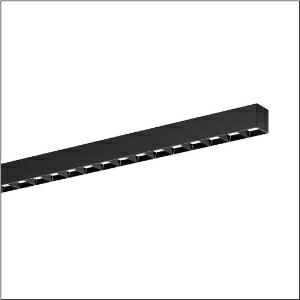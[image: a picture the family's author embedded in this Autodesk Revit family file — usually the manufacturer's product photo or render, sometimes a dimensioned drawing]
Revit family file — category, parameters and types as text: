
# Revit family: silica_r__21_51mx24dc3abb_157e
name_source: partatom
category: Lighting Fixtures
units: mm (PartAtom-declared; Revit-internal decimal feet)

## family parameters
Cut with Voids When Loaded = No
Host = Face
Light Source = No
Part Type = Normal
Room Calculation Point = No
Round Connector Dimension = Use Diameter
Shared = No

## types (1)
- --- (1 x LED, 10800 lm, 79 W, 3000K)
    Apparent Load = 79 VA
    CIE Flux Codes = 74 94 99 100 100
    Color Rendering = 80
    Color Temperature = 3000K
    Default Elevation = 1800 mm
    Description = Silica® 21, office luminaire, primary light control with darklight reflector, of PMMA, black, CAT 2 (L<= 3000cd/m²), light emission: direct distribution, primary light characteristic: asymmetric, installation type: surface-mounted, LED, rated luminous flux: 10.800lm, luminous efficacy: 137lm/W, light colour: 830, colour temperature: 3000K, with terminal, 3+2-pole, max. 2.5mm², mains connection: 220..240V, AC, 50/60Hz, rated input power: 79W, luminaire housing, of aluminium, jet black (RAL 9005), length: 3.004mm, width: 53mm, height: 53mm, protection rating (complete): IP20, insulation class (complete): insulation class I (protective earthing), certification: CE, permissible operating ambient temperature: 0..+35°C, standard: EN 50419, packaging unit: 1 piece
    Height = 0 mm  [stored 0 ft]
    Lamp = 1 x LED
    Lamp Light Flux = 10800 lm
    Lamp Power = 79 W
    Lamp count = 1
    Length = 3004 mm
    Luminous efficacy = 137 lm/W
    Manufacturer = Siteco
    ModVariant = No
    Model = 51MX24DC3ABB
    Mounting Place = Ceiling
    Mounting Type = Recessed
    Number of Poles = 1
    OnlyDefault = Yes
    Power Factor = 1
    Product Name = Silica® 21
    Product group = office luminaire | ceiling recessed
    ProductGroupID = 401
    Protection Class = Protection class I
    Protection Degree = IP 20
    RLX_Detail_Level = 1
    RLX_Emergency_Light_Flux = 0 lm
    RLX_Emergency_Type = 0
    RLX_Emergency_Type_DB = No
    RlxData = <blob elided: 64549 chars, md5=4339ba03>
    Socket = socket
    Standby Power = 0 W
    System Light Flux = 10800 lm
    System Power = 79 W
    Type Comments = factory setting: luminous flux: 100 % | dim-lin: 254 | 448 mA
    Type Image = l_1297756.jpg
    URL = http://relux.com
    VarID = @adj_053519
    Voltage = 0 V
    Weight = 0.00 kg
    Width = 53 mm

note: [stored X ft] marks values corroborated as IEEE doubles in the binary element streams (Revit-internal decimal feet)

## geometry (parser evidence)
native form markers: Blend x4, Sweep x10
no freeform markers — native parametric forms only
